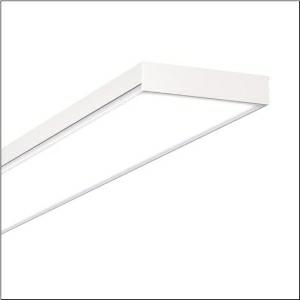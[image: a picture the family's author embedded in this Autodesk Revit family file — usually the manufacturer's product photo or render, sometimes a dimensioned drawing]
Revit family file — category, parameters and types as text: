
# Revit family: apollon_r__31_surface_51mp26wd2441wa_9052
name_source: partatom
category: Lighting Fixtures
units: mm (PartAtom-declared; Revit-internal decimal feet)

## family parameters
Cut with Voids When Loaded = No
Host = Face
Light Source = No
Part Type = Normal
Room Calculation Point = No
Round Connector Dimension = Use Diameter
Shared = No

## types (1)
- Apollon® 31 Surface (1 x LED, 4600 lm, 33 W, 4000K)
    Apparent Load = 33 VA
    CIE Flux Codes = 61 87 97 97 100
    Color Rendering = 80
    Color Temperature = 4000K
    Default Elevation = 1800 mm
    Description = Apollon® 31 Surface, office luminaire, primary optical cover: micro prismatic cover, of PMMA, light emission: direct distribution, primary light characteristic: symmetric, installation type: surface-mounted, LED, rated luminous flux: 4.600lm, luminous efficacy: 139lm/W, light colour: 840, colour temperature: 4000K, control gear: DALI 2, with terminal, 5-pole, mains connection: 220..240V, AC, 50/60Hz, rated input power: 33W, housing, of sheet steel, coil coated, traffic white (RAL 9016), length: 1.545mm, width: 200mm, height: 44mm, protection rating (complete): IP20, insulation class (complete): insulation class II (safety insulation), certification: CE, impact resistance: IK02, permissible operating ambient temperature: -20..+40°C, standard: EN 60598-2-22, packaging unit: 1 piece
    Height = 44 mm
    Lamp = 1 x LED
    Lamp Light Flux = 4600 lm
    Lamp Power = 33 W
    Lamp count = 1
    Length = 1545 mm
    Luminous efficacy = 139 lm/W
    Manufacturer = Siteco
    ModVariant = No
    Model = 51MP26WD2441WA
    Mounting Place = Ceiling
    Mounting Type = Surface mounted
    Number of Poles = 1
    OnlyDefault = Yes
    Power Factor = 1
    Product Name = Apollon® 31 Surface
    Product group = office luminaire | ceiling mounted
    ProductGroupID = 302
    Protection Class = Protection class II
    Protection Degree = IP 20
    RLX_Detail_Level = 1
    RLX_Emergency_Light_Flux = 0 lm
    RLX_Emergency_Type = 0
    RLX_Emergency_Type_DB = No
    RlxData = <blob elided: 20777 chars, md5=7ee0de83>
    Socket = socket
    Standby Power = 0 W
    System Light Flux = 4600 lm
    System Power = 33 W
    Type Comments = Product without accessories
    Type Image = l_1313658.jpg
    URL = http://relux.com
    VarID = ---
    Voltage = 0 V
    Weight = 0.00 kg
    Width = 200 mm  [stored 0.656168 ft]

note: [stored X ft] marks values corroborated as IEEE doubles in the binary element streams (Revit-internal decimal feet)

## geometry (parser evidence)
native form markers: Blend x4, Sweep x9
no freeform markers — native parametric forms only
